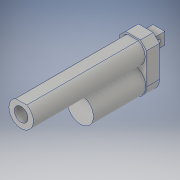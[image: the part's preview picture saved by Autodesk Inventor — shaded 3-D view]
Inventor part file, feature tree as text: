
AUTODESK INVENTOR PART (.ipt)
format: ipt  version: 2019.4 (Build 234330000, 330)  size: 165,376 bytes
history: native  units: mm
features: extrude x6, sketch x2, hole x1
ambient origin geometry x8: Origin, YZ Plane, XZ Plane, XY Plane, X Axis, Y Axis, Z Axis, Center Point
bodies: Solid1 (feature_tree)
feature tree (9):
  sketch  "Sketch1"  dims[d0=40.0mm d1=74.8mm]
  extrude  "Extrusion1"  Depth=40.0mm
  extrude  "Extrusion2"  Depth=20.0mm
  extrude  "Extrusion3"  Depth=17.5mm
  extrude  "Extrusion5"  Depth=17.5mm
  extrude  "Extrusion6"  Depth=2.0mm
  extrude  "Extrusion7"  Depth=9.15mm
  hole  "Hole1"  [1 undecoded]
  sketch  "Sketch2"  dims[d2=38.0mm d3=20.0mm d4=17.5mm d5=17.5mm d6=35.8mm d7=9.15mm d8=9.15mm d9=9.15mm d10=9.15mm d11=9.15mm d12=45.65mm d13=95.7mm d14=0.0mm d15=19.0mm d16=0.0mm d17=19.0mm d18=0.0mm d21=20.0mm d22=2.0mm d23=182.5mm d24=0.0mm d25=182.5mm d26=0.0mm d27=32.5mm d28=0.0mm d29=10.0mm d30=6.0mm d31=6.0mm d32=4.0mm d33=2.0mm d34=90.0deg d35=8.0mm d36=20.594885mm]
note: 1 required parameter value undecoded (feature->parameter linkage not recoverable at this tier; creation-order binding heuristic only, values carry confidence <= 0.55)
